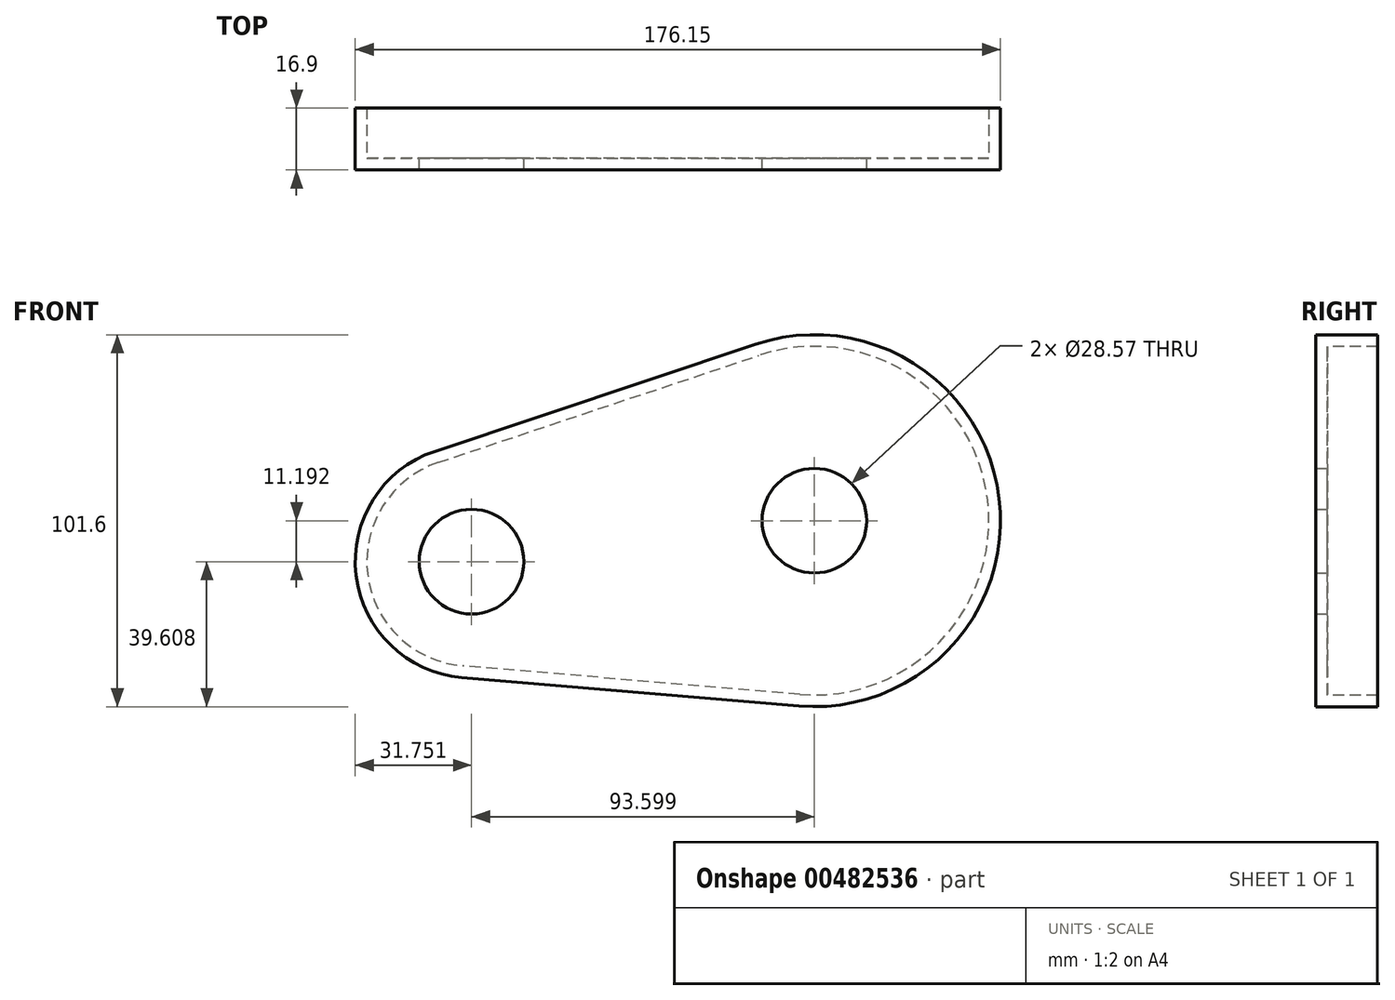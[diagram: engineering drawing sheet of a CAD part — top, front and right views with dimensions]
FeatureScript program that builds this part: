
annotation { "Feature Type Name" : "Feature", "Feature Type Description" : "" }
export const myFeature = defineFeature(function(context is Context, id is Id, definition is map)
    precondition{}
    {
        {
            var Q0;
            Q0=qCreatedBy(makeId("Front.planeOp"),FACE);
            var sketch = newSketch(context, id + "F0", { "sketchPlane" : qUnion([Q0])});
            skArc(sketch, "E0", {"start": v(-4.29, -50.62) * mm, "mid": v(50.44, 6.03) * mm, "end": v(-16.1, 48.18) * mm});
            skCircle(sketch, "E1", {"center": v(0, 0) * mm, "radius": 14.29 * mm});
            skArc(sketch, "E2", {"start": v(-103.66, 18.92) * mm, "mid": v(-125.35, -11.37) * mm, "end": v(-103.33, -41.42) * mm});
            skLineSegment(sketch, "E3", {"start": v(-16.1, 48.18) * mm, "end": v(-103.66, 18.92) * mm});
            skLineSegment(sketch, "E4.0", {"start": v(-15.1, 45.17) * mm, "end": v(-102.66, 15.9) * mm});
            skArc(sketch, "E4.1", {"start": v(-4.02, -47.46) * mm, "mid": v(47.29, 5.65) * mm, "end": v(-15.1, 45.17) * mm});
            skArc(sketch, "E4.3", {"start": v(-102.66, 15.9) * mm, "mid": v(-121.97, -14.59) * mm, "end": v(-96.01, -39.67) * mm});
            skCircle(sketch, "E5", {"center": v(-93.6, -11.2) * mm, "radius": 14.29 * mm});
            skLineSegment(sketch, "E6", {"start": v(-4.29, -50.62) * mm, "end": v(-96.28, -42.83) * mm});
            skArc(sketch, "E7", {"start": v(-103.66, 18.92) * mm, "mid": v(-125.12, -14.96) * mm, "end": v(-96.28, -42.83) * mm});
            skLineSegment(sketch, "E8.0", {"start": v(-4.02, -47.46) * mm, "end": v(-96.01, -39.67) * mm});
            skSolve(sketch);
        }
        {
            var Q0;
            Q0=makeQuery(id+"F0.imprint","IMPRINT",FACE,{"disambiguationData":[TD([[makeQuery(id+"F0.imprint","IMPRINT",EDGE,{"derivedFrom":sQuery(id+"F0.wireOp",EDGE,"fnuw4xRw-q3RJ-6Wpu-261c-KhJfibXVhHQk")}),1.0]])]});
            var Q1;
            Q1=makeQuery(id+"F0.imprint","IMPRINT",FACE,{"disambiguationData":[TD([[makeQuery(id+"F0.imprint","IMPRINT",EDGE,{"derivedFrom":sQuery(id+"F0.wireOp",EDGE,"E0")}),1.0]])]});
            var Q2;
            Q2=makeQuery(id+"F0.imprint","IMPRINT",FACE,{"disambiguationData":[TD([[makeQuery(id+"F0.imprint","IMPRINT",EDGE,{"derivedFrom":sQuery(id+"F0.wireOp",EDGE,"E1")}),-1.0]])]});
            extrude(context, id + "F1", {"entities" : qUnion([Q0, Q1, Q2]), "depth" : 3.17 * mm});
        }
        {
            var Q0;
            Q0=makeQuery(id+"F1.opExtrude","CAP_FACE",FACE,{"disambiguationData":[OSD([sQuery(id+"F0.wireOp",EDGE,"E0"),sQuery(id+"F0.wireOp",EDGE,"E1"),sQuery(id+"F0.wireOp",EDGE,"E3"),sQuery(id+"F0.wireOp",EDGE,"E5"),sQuery(id+"F0.wireOp",EDGE,"E6"),sQuery(id+"F0.wireOp",EDGE,"E7")])],"isStart":true});
            var sketch = newSketch(context, id + "F2", { "sketchPlane" : qUnion([Q0])});
            skLineSegment(sketch, "E9.0", {"start": v(102.66, 15.9) * mm, "end": v(15.1, 45.17) * mm});
            skArc(sketch, "E9.1", {"start": v(96.01, -39.67) * mm, "mid": v(121.97, -14.59) * mm, "end": v(102.66, 15.9) * mm});
            skLineSegment(sketch, "E9.2", {"start": v(4.02, -47.46) * mm, "end": v(96.01, -39.67) * mm});
            skArc(sketch, "E9.3", {"start": v(15.1, 45.17) * mm, "mid": v(-47.29, 5.65) * mm, "end": v(4.02, -47.46) * mm});
            skSolve(sketch);
        }
        {
            var Q0;
            Q0=makeQuery(id+"F2.imprint","IMPRINT",FACE,{"disambiguationData":[TD([[makeQuery(id+"F2.imprint","IMPRINT",EDGE,{"derivedFrom":sQuery(id+"F2.wireOp",EDGE,"E9.0")}),-1.0]])]});
            extrude(context, id + "F3", {"entities" : qUnion([Q0]), "operationType" : NewBodyOperationType.ADD, "depth" : 13.72 * mm});
        }
    });
